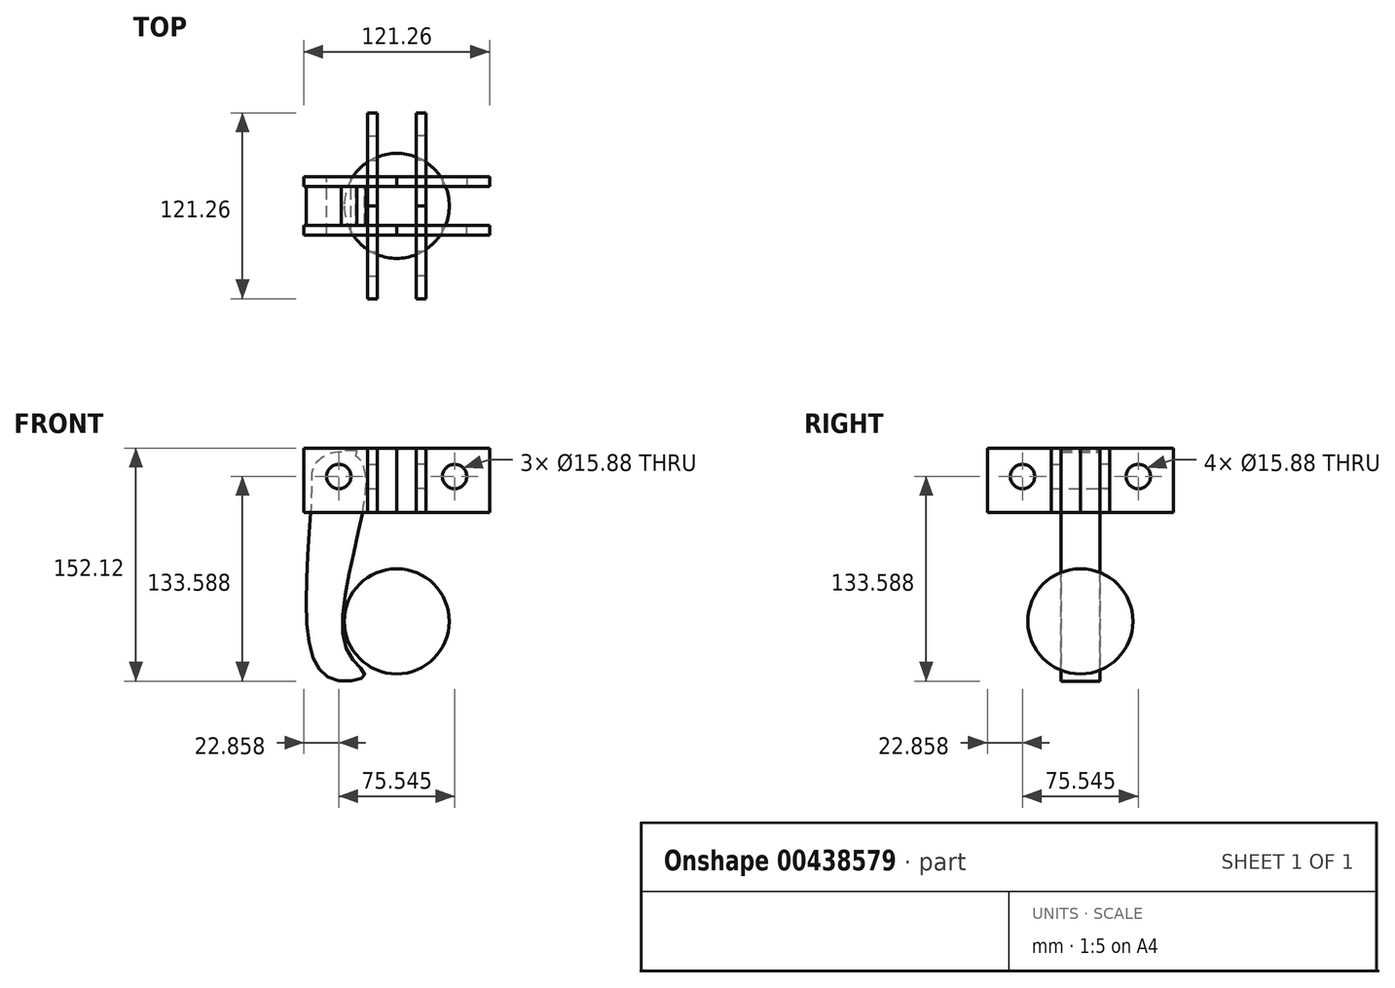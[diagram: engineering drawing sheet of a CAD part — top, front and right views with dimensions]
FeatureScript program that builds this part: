
annotation { "Feature Type Name" : "Feature", "Feature Type Description" : "" }
export const myFeature = defineFeature(function(context is Context, id is Id, definition is map)
    precondition{}
    {
        {
            var Q0;
            Q0=qCreatedBy(makeId("Front.planeOp"),FACE);
            var sketch = newSketch(context, id + "F0", { "sketchPlane" : qUnion([Q0])});
            skCircle(sketch, "E0", {"center": v(0, -32.54) * mm, "radius": 34.3 * mm, "construction": true});
            skFitSpline(sketch, "E1", {"points": [v(-39.95, 77.72) * mm, v(-53.53, 69.57) * mm, v(-55.7, 50) * mm, v(-57.88, -42.4) * mm, v(-40.49, -70.65) * mm, v(-20.92, -67.94) * mm, v(-32.34, -51.63) * mm, v(-25.27, 24.46) * mm, v(-23.32, 71.96) * mm, v(-39.95, 77.72) * mm]});
            skCircle(sketch, "E2", {"center": v(-37.77, 61.96) * mm, "radius": 7.94 * mm});
            skSolve(sketch);
        }
        {
            var Q0;
            Q0=makeQuery(id+"F0.imprint","IMPRINT",FACE,{"disambiguationData":[TD([[makeQuery(id+"F0.imprint","IMPRINT",EDGE,{"derivedFrom":sQuery(id+"F0.wireOp",EDGE,"E1")}),1.0]])]});
            extrude(context, id + "F1", {"entities" : qUnion([Q0]), "endBound" : BoundingType.SYMMETRIC, "depth" : 25.4 * mm});
        }
        {
            var Q0;
            Q0=makeQuery(id+"F1.opExtrude","CAP_FACE",FACE,{"disambiguationData":[OSD([sQuery(id+"F0.wireOp",EDGE,"E1"),sQuery(id+"F0.wireOp",EDGE,"E2")])],"isStart":false});
            var sketch = newSketch(context, id + "F2", { "sketchPlane" : qUnion([Q0])});
            skLineSegment(sketch, "E3.bottom", {"start": v(-60.63, 80.5) * mm, "end": v(0, 80.5) * mm});
            skLineSegment(sketch, "E3.top", {"start": v(-60.63, 38.66) * mm, "end": v(0, 38.66) * mm});
            skLineSegment(sketch, "E3.left", {"start": v(-60.63, 80.5) * mm, "end": v(-60.63, 38.66) * mm});
            skLineSegment(sketch, "E3.right", {"start": v(0, 80.5) * mm, "end": v(0, 38.66) * mm});
            skSolve(sketch);
        }
        {
            var Q0;
            Q0=makeQuery(id+"F2.imprint","IMPRINT",FACE,{"disambiguationData":[TD([[makeQuery(id+"F2.imprint","IMPRINT",EDGE,{"derivedFrom":makeQuery(id+"F1.opExtrude","CAP_EDGE",EDGE,{"disambiguationData":[OSD([sQuery(id+"F0.wireOp",EDGE,"E2")])],"isStart":false})}),-1.0]])]});
            var Q1;
            Q1=makeQuery(id+"F2.imprint","IMPRINT",FACE,{"disambiguationData":[TD([[makeQuery(id+"F2.imprint","IMPRINT",EDGE,{"derivedFrom":sQuery(id+"F2.wireOp",EDGE,"E3.bottom")}),-1.0]])]});
            extrude(context, id + "F3", {"entities" : qUnion([Q0, Q1]), "depth" : 6.35 * mm});
        }
        {
            var Q0;
            Q0=makeQuery(id+"F3.opExtrude","SWEPT_BODY",BODY,{"disambiguationData":[OSD([sQuery(id+"F0.wireOp",EDGE,"E2"),sQuery(id+"F2.wireOp",EDGE,"E3.bottom"),sQuery(id+"F2.wireOp",EDGE,"E3.top"),sQuery(id+"F2.wireOp",EDGE,"E3.left"),sQuery(id+"F2.wireOp",EDGE,"E3.right")])]});
            var Q1;
            Q1=qCreatedBy(makeId("Front.planeOp"),FACE);
            mirror(context, id + "F4", {"entities" : qUnion([Q0]), "mirrorPlane" : qUnion([Q1])});
        }
        {
            var Q0;
            Q0=makeQuery(id+"F3.opExtrude","SWEPT_BODY",BODY,{"disambiguationData":[OSD([sQuery(id+"F0.wireOp",EDGE,"E2"),sQuery(id+"F2.wireOp",EDGE,"E3.bottom"),sQuery(id+"F2.wireOp",EDGE,"E3.top"),sQuery(id+"F2.wireOp",EDGE,"E3.left"),sQuery(id+"F2.wireOp",EDGE,"E3.right")])]});
            var Q1;
            Q1=makeQuery(id+"F4.opPattern","COPY",BODY,{"derivedFrom":makeQuery(id+"F3.opExtrude","SWEPT_BODY",BODY,{"disambiguationData":[OSD([sQuery(id+"F0.wireOp",EDGE,"E2"),sQuery(id+"F2.wireOp",EDGE,"E3.bottom"),sQuery(id+"F2.wireOp",EDGE,"E3.top"),sQuery(id+"F2.wireOp",EDGE,"E3.left"),sQuery(id+"F2.wireOp",EDGE,"E3.right")])]}),"instanceName":"1"});
            var Q2;
            Q2=qCreatedBy(makeId("Right.planeOp"),FACE);
            mirror(context, id + "F5", {"entities" : qUnion([Q0, Q1]), "mirrorPlane" : qUnion([Q2])});
        }
        {
            var Q0;
            Q0=qCreatedBy(makeId("Right.planeOp"),FACE);
            var sketch = newSketch(context, id + "F6", { "sketchPlane" : qUnion([Q0])});
            skLineSegment(sketch, "E4", {"start": v(0, 0) * mm, "end": v(0, 81.71) * mm});
            skSolve(sketch);
        }
        {
            var Q0;
            Q0=makeQuery(id+"F3.opExtrude","SWEPT_BODY",BODY,{"disambiguationData":[OSD([sQuery(id+"F0.wireOp",EDGE,"E2"),sQuery(id+"F2.wireOp",EDGE,"E3.bottom"),sQuery(id+"F2.wireOp",EDGE,"E3.top"),sQuery(id+"F2.wireOp",EDGE,"E3.left"),sQuery(id+"F2.wireOp",EDGE,"E3.right")])]});
            var Q1;
            Q1=makeQuery(id+"F4.opPattern","COPY",BODY,{"derivedFrom":makeQuery(id+"F3.opExtrude","SWEPT_BODY",BODY,{"disambiguationData":[OSD([sQuery(id+"F0.wireOp",EDGE,"E2"),sQuery(id+"F2.wireOp",EDGE,"E3.bottom"),sQuery(id+"F2.wireOp",EDGE,"E3.top"),sQuery(id+"F2.wireOp",EDGE,"E3.left"),sQuery(id+"F2.wireOp",EDGE,"E3.right")])]}),"instanceName":"1"});
            var Q2;
            Q2=makeQuery(id+"F5.opPattern","COPY",BODY,{"derivedFrom":makeQuery(id+"F3.opExtrude","SWEPT_BODY",BODY,{"disambiguationData":[OSD([sQuery(id+"F0.wireOp",EDGE,"E2"),sQuery(id+"F2.wireOp",EDGE,"E3.bottom"),sQuery(id+"F2.wireOp",EDGE,"E3.top"),sQuery(id+"F2.wireOp",EDGE,"E3.left"),sQuery(id+"F2.wireOp",EDGE,"E3.right")])]}),"instanceName":"1"});
            var Q3;
            Q3=makeQuery(id+"F5.opPattern","COPY",BODY,{"derivedFrom":makeQuery(id+"F4.opPattern","COPY",BODY,{"derivedFrom":makeQuery(id+"F3.opExtrude","SWEPT_BODY",BODY,{"disambiguationData":[OSD([sQuery(id+"F0.wireOp",EDGE,"E2"),sQuery(id+"F2.wireOp",EDGE,"E3.bottom"),sQuery(id+"F2.wireOp",EDGE,"E3.top"),sQuery(id+"F2.wireOp",EDGE,"E3.left"),sQuery(id+"F2.wireOp",EDGE,"E3.right")])]}),"instanceName":"1"}),"instanceName":"1"});
            var Q4;
            Q4=sQuery(id+"F6.wireOp",EDGE,"E4");
            circularPattern(context, id + "F7", {"entities" : qUnion([Q0, Q1, Q2, Q3]), "axis" : qUnion([Q4]), "angle" : 90 * degree, "instanceCount" : 2, "equalSpace" : true});
        }
        {
            var Q0;
            Q0=qCreatedBy(makeId("Front.planeOp"),FACE);
            var sketch = newSketch(context, id + "F8", { "sketchPlane" : qUnion([Q0])});
            skCircle(sketch, "E5.0", {"center": v(0, -32.54) * mm, "radius": 34.3 * mm});
            skLineSegment(sketch, "E6", {"start": v(0, 1.75) * mm, "end": v(0, -66.83) * mm});
            skSolve(sketch);
        }
        {
            var Q0;
            {var subQ0=sQuery(id+"F8.wireOp",EDGE,"E6");Q0=makeQuery(id+"F8.imprint","IMPRINT",FACE,{"disambiguationData":[TD([[makeQuery(id+"F8.imprint","IMPRINT",EDGE,{"derivedFrom":subQ0}),1.0]])]});}
            var Q1;
            Q1=sQuery(id+"F8.wireOp",EDGE,"E6");
            revolve(context, id + "F9", {"entities" : qUnion([Q0]), "axis" : qUnion([Q1]), "revolveType" : RevolveType.FULL});
        }
        {
            var Q0;
            Q0=makeQuery(id+"F1.opExtrude","CAP_FACE",FACE,{"disambiguationData":[OSD([sQuery(id+"F0.wireOp",EDGE,"E1"),sQuery(id+"F0.wireOp",EDGE,"E2")])],"isStart":false});
            var sketch = newSketch(context, id + "F10", { "sketchPlane" : qUnion([Q0])});
            skLineSegment(sketch, "E7", {"start": v(-36.16, 77.99) * mm, "end": v(-32.62, 90.55) * mm});
            skLineSegment(sketch, "E8", {"start": v(-23.45, 87.96) * mm, "end": v(-26.98, 75.44) * mm});
            skArc(sketch, "E9", {"start": v(-32.62, 90.55) * mm, "mid": v(-26.74, 93.84) * mm, "end": v(-23.45, 87.96) * mm});
            skCircle(sketch, "E10", {"center": v(-28.03, 89.25) * mm, "radius": 2.67 * mm});
            skFitSpline(sketch, "E11.0", {"points": [v(-39.95, 77.72) * mm, v(-45.82, 76.78) * mm, v(-56.96, 69.84) * mm, v(-53.8, 48.76) * mm, v(-64.5, -42.38) * mm, v(-46.54, -75.15) * mm, v(-11.35, -69.3) * mm, v(-44.88, -51.3) * mm, v(-24.3, 23.05) * mm, v(-15.6, 74.4) * mm, v(-33.76, 78.7) * mm, v(-39.95, 77.72) * mm]});
            skSolve(sketch);
        }
        {
            var Q0;
            {var subQ1=sQuery(id+"F10.wireOp",EDGE,"E7");Q0=makeQuery(id+"F10.imprint","IMPRINT",FACE,{"disambiguationData":[TD([[makeQuery(id+"F10.imprint","IMPRINT",EDGE,{"derivedFrom":subQ1}),-1.0]])]});}
            var Q1;
            Q1=makeQuery(id+"F1.opExtrude","CAP_FACE",FACE,{"disambiguationData":[OSD([sQuery(id+"F0.wireOp",EDGE,"E1"),sQuery(id+"F0.wireOp",EDGE,"E2")])],"isStart":true});
            extrude(context, id + "F11", {"entities" : qUnion([Q0]), "operationType" : NewBodyOperationType.ADD, "oppositeDirection" : true, "endBoundEntityFace" : qUnion([Q1]), "depth" : 25.4 * mm});
        }
    });
